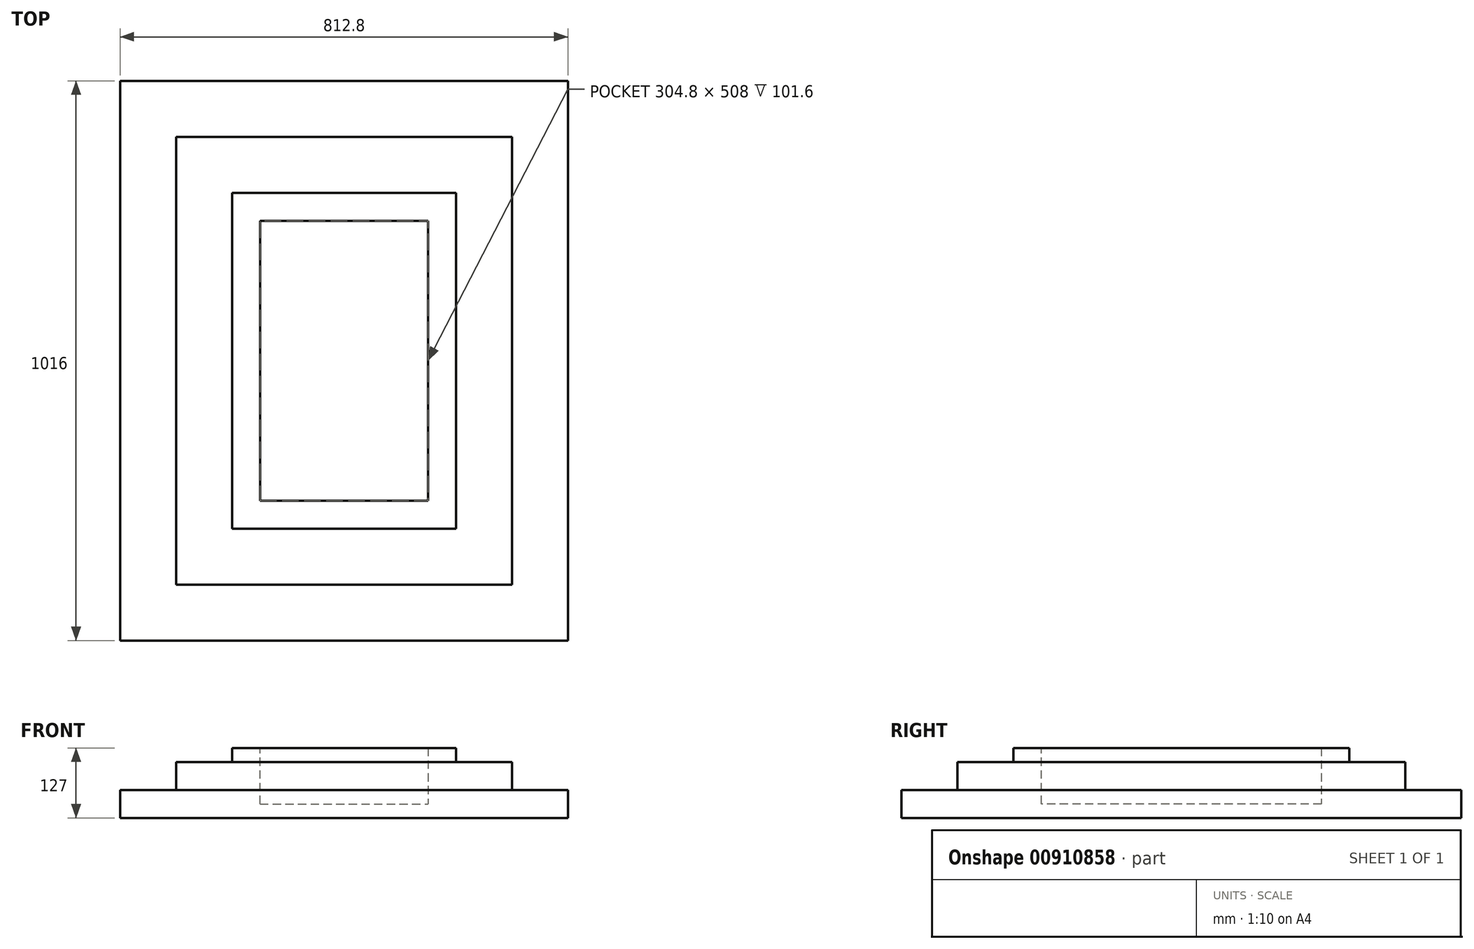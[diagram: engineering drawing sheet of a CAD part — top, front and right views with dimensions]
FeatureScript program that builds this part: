
annotation { "Feature Type Name" : "Feature", "Feature Type Description" : "" }
export const myFeature = defineFeature(function(context is Context, id is Id, definition is map)
    precondition{}
    {
        {
            var Q0;
            Q0=qCreatedBy(makeId("Front.planeOp"),FACE);
            var sketch = newSketch(context, id + "F0", { "sketchPlane" : qUnion([Q0])});
            skLineSegment(sketch, "E0.bottom", {"start": v(-203.2, -50.8) * mm, "end": v(203.2, -50.8) * mm});
            skLineSegment(sketch, "E0.top", {"start": v(-203.2, 50.8) * mm, "end": v(203.2, 50.8) * mm});
            skLineSegment(sketch, "E0.left", {"start": v(-203.2, -50.8) * mm, "end": v(-203.2, 50.8) * mm});
            skLineSegment(sketch, "E0.right", {"start": v(203.2, -50.8) * mm, "end": v(203.2, 50.8) * mm});
            skPoint(sketch, "E0.middle", {"position": v(0, 0) * mm});
            skSolve(sketch);
        }
        {
            var Q0;
            Q0 = qSketchRegion(id + "F0", true);
            extrude(context, id + "F1", {"entities" : qUnion([Q0]), "endBound" : BoundingType.SYMMETRIC, "depth" : 50.8 * mm, "offsetDistance" : 25.4 * mm});
        }
        {
            var Q0;
            Q0=makeQuery(id+"F1.opExtrude","CAP_FACE",FACE,{"disambiguationData":[OSD([sQuery(id+"F0.wireOp",EDGE,"E0.bottom"),sQuery(id+"F0.wireOp",EDGE,"E0.top"),sQuery(id+"F0.wireOp",EDGE,"E0.left"),sQuery(id+"F0.wireOp",EDGE,"E0.right")])],"isStart":true});
            var sketch = newSketch(context, id + "F2", { "sketchPlane" : qUnion([Q0])});
            skLineSegment(sketch, "E1.bottom", {"start": v(-203.2, 50.8) * mm, "end": v(-152.4, 50.8) * mm});
            skLineSegment(sketch, "E1.top", {"start": v(-203.2, -50.8) * mm, "end": v(-152.4, -50.8) * mm});
            skLineSegment(sketch, "E1.left", {"start": v(-203.2, 50.8) * mm, "end": v(-203.2, -50.8) * mm});
            skLineSegment(sketch, "E1.right", {"start": v(-152.4, 50.8) * mm, "end": v(-152.4, -50.8) * mm});
            skLineSegment(sketch, "E2.bottom", {"start": v(203.2, -50.8) * mm, "end": v(152.4, -50.8) * mm});
            skLineSegment(sketch, "E2.top", {"start": v(203.2, 50.8) * mm, "end": v(152.4, 50.8) * mm});
            skLineSegment(sketch, "E2.left", {"start": v(203.2, -50.8) * mm, "end": v(203.2, 50.8) * mm});
            skLineSegment(sketch, "E2.right", {"start": v(152.4, -50.8) * mm, "end": v(152.4, 50.8) * mm});
            skSolve(sketch);
        }
        {
            var Q0;
            Q0 = qSketchRegion(id + "F2", true);
            extrude(context, id + "F3", {"entities" : qUnion([Q0]), "operationType" : NewBodyOperationType.ADD, "depth" : 508 * mm, "offsetDistance" : 25.4 * mm});
        }
        {
            var Q0;
            Q0=makeQuery(id+"F3.opExtrude","CAP_FACE",FACE,{"disambiguationData":[OSD([sQuery(id+"F2.wireOp",EDGE,"E1.bottom"),sQuery(id+"F2.wireOp",EDGE,"E1.top"),sQuery(id+"F2.wireOp",EDGE,"E1.left"),sQuery(id+"F2.wireOp",EDGE,"E1.right")])],"isStart":false});
            var sketch = newSketch(context, id + "F4", { "sketchPlane" : qUnion([Q0])});
            skLineSegment(sketch, "E3.bottom", {"start": v(-203.2, 50.8) * mm, "end": v(203.2, 50.8) * mm});
            skLineSegment(sketch, "E3.top", {"start": v(-203.2, -50.8) * mm, "end": v(203.2, -50.8) * mm});
            skLineSegment(sketch, "E3.left", {"start": v(-203.2, 50.8) * mm, "end": v(-203.2, -50.8) * mm});
            skLineSegment(sketch, "E3.right", {"start": v(203.2, 50.8) * mm, "end": v(203.2, -50.8) * mm});
            skSolve(sketch);
        }
        {
            var Q0;
            Q0 = qSketchRegion(id + "F4", true);
            extrude(context, id + "F5", {"entities" : qUnion([Q0]), "operationType" : NewBodyOperationType.ADD, "depth" : 50.8 * mm, "offsetDistance" : 25.4 * mm});
        }
        {
            var Q0;
            Q0=makeQuery(id+"F5.boolean.opBoolean","MERGE",FACE,{"derivedFrom":[makeQuery(id+"F3.boolean.opBoolean","MERGE",FACE,{"derivedFrom":[makeQuery(id+"F1.opExtrude","SWEPT_FACE",FACE,{"disambiguationData":[OSD([sQuery(id+"F0.wireOp",EDGE,"E0.bottom")])]}),makeQuery(id+"F3.opExtrude","SWEPT_FACE",FACE,{"disambiguationData":[OSD([sQuery(id+"F2.wireOp",EDGE,"E1.top")])]}),makeQuery(id+"F3.opExtrude","SWEPT_FACE",FACE,{"disambiguationData":[OSD([sQuery(id+"F2.wireOp",EDGE,"E2.bottom")])]})]}),makeQuery(id+"F5.opExtrude","SWEPT_FACE",FACE,{"disambiguationData":[OSD([sQuery(id+"F4.wireOp",EDGE,"E3.top")])]})]});
            var sketch = newSketch(context, id + "F6", { "sketchPlane" : qUnion([Q0])});
            skLineSegment(sketch, "E4.bottom", {"start": v(-203.2, 25.4) * mm, "end": v(203.2, 25.4) * mm});
            skLineSegment(sketch, "E4.top", {"start": v(-203.2, -584.2) * mm, "end": v(203.2, -584.2) * mm});
            skLineSegment(sketch, "E4.left", {"start": v(-203.2, 25.4) * mm, "end": v(-203.2, -584.2) * mm});
            skLineSegment(sketch, "E4.right", {"start": v(203.2, 25.4) * mm, "end": v(203.2, -584.2) * mm});
            skSolve(sketch);
        }
        {
            var Q0;
            Q0 = qSketchRegion(id + "F6", true);
            extrude(context, id + "F7", {"entities" : qUnion([Q0]), "operationType" : NewBodyOperationType.ADD, "depth" : 25.4 * mm, "offsetDistance" : 25.4 * mm});
        }
        {
            var Q0;
            Q0=makeQuery(id+"F7.boolean.opBoolean","MERGE",FACE,{"derivedFrom":[makeQuery(id+"F1.opExtrude","CAP_FACE",FACE,{"disambiguationData":[OSD([sQuery(id+"F0.wireOp",EDGE,"E0.bottom"),sQuery(id+"F0.wireOp",EDGE,"E0.top"),sQuery(id+"F0.wireOp",EDGE,"E0.left"),sQuery(id+"F0.wireOp",EDGE,"E0.right")])],"isStart":false}),makeQuery(id+"F7.opExtrude","SWEPT_FACE",FACE,{"disambiguationData":[OSD([sQuery(id+"F6.wireOp",EDGE,"E4.bottom")])]})]});
            var sketch = newSketch(context, id + "F8", { "sketchPlane" : qUnion([Q0])});
            skLineSegment(sketch, "E5.bottom", {"start": v(-203.2, -76.2) * mm, "end": v(203.2, -76.2) * mm});
            skLineSegment(sketch, "E5.top", {"start": v(-203.2, -25.4) * mm, "end": v(203.2, -25.4) * mm});
            skLineSegment(sketch, "E5.left", {"start": v(-203.2, -76.2) * mm, "end": v(-203.2, -25.4) * mm});
            skLineSegment(sketch, "E5.right", {"start": v(203.2, -76.2) * mm, "end": v(203.2, -25.4) * mm});
            skLineSegment(sketch, "E6.top", {"start": v(-203.2, 25.4) * mm, "end": v(203.2, 25.4) * mm});
            skLineSegment(sketch, "E6.left", {"start": v(-203.2, -25.4) * mm, "end": v(-203.2, 25.4) * mm});
            skLineSegment(sketch, "E6.right", {"start": v(203.2, -25.4) * mm, "end": v(203.2, 25.4) * mm});
            skSolve(sketch);
        }
        {
            var Q0;
            Q0=makeQuery(id+"F8.imprint","IMPRINT",FACE,{"disambiguationData":[TD([[makeQuery(id+"F8.imprint","IMPRINT",EDGE,{"derivedFrom":sQuery(id+"F8.wireOp",EDGE,"E5.bottom")}),1.0]])]});
            extrude(context, id + "F9", {"entities" : qUnion([Q0]), "operationType" : NewBodyOperationType.ADD, "depth" : 203.2 * mm, "offsetDistance" : 25.4 * mm});
        }
        {
            var Q0;
            Q0=makeQuery(id+"F7.boolean.opBoolean","MERGE",FACE,{"derivedFrom":[makeQuery(id+"F1.opExtrude","CAP_FACE",FACE,{"disambiguationData":[OSD([sQuery(id+"F0.wireOp",EDGE,"E0.bottom"),sQuery(id+"F0.wireOp",EDGE,"E0.top"),sQuery(id+"F0.wireOp",EDGE,"E0.left"),sQuery(id+"F0.wireOp",EDGE,"E0.right")])],"isStart":false}),makeQuery(id+"F7.opExtrude","SWEPT_FACE",FACE,{"disambiguationData":[OSD([sQuery(id+"F6.wireOp",EDGE,"E4.bottom")])]})]});
            var sketch = newSketch(context, id + "F10", { "sketchPlane" : qUnion([Q0])});
            skLineSegment(sketch, "E7.bottom", {"start": v(-203.2, -25.4) * mm, "end": v(203.2, -25.4) * mm});
            skLineSegment(sketch, "E7.top", {"start": v(-203.2, 25.4) * mm, "end": v(203.2, 25.4) * mm});
            skLineSegment(sketch, "E7.left", {"start": v(-203.2, -25.4) * mm, "end": v(-203.2, 25.4) * mm});
            skLineSegment(sketch, "E7.right", {"start": v(203.2, -25.4) * mm, "end": v(203.2, 25.4) * mm});
            skSolve(sketch);
        }
        {
            var Q0;
            Q0 = qSketchRegion(id + "F10", true);
            extrude(context, id + "F11", {"entities" : qUnion([Q0]), "operationType" : NewBodyOperationType.ADD, "depth" : 101.6 * mm, "offsetDistance" : 25.4 * mm});
        }
        {
            var Q0;
            Q0=makeQuery(id+"F7.boolean.opBoolean","MERGE",FACE,{"derivedFrom":[makeQuery(id+"F5.opExtrude","CAP_FACE",FACE,{"disambiguationData":[OSD([sQuery(id+"F4.wireOp",EDGE,"E3.bottom"),sQuery(id+"F4.wireOp",EDGE,"E3.top"),sQuery(id+"F4.wireOp",EDGE,"E3.left"),sQuery(id+"F4.wireOp",EDGE,"E3.right")])],"isStart":false}),makeQuery(id+"F7.opExtrude","SWEPT_FACE",FACE,{"disambiguationData":[OSD([sQuery(id+"F6.wireOp",EDGE,"E4.top")])]})]});
            var sketch = newSketch(context, id + "F12", { "sketchPlane" : qUnion([Q0])});
            skLineSegment(sketch, "E8.bottom", {"start": v(-203.2, -76.2) * mm, "end": v(203.2, -76.2) * mm});
            skLineSegment(sketch, "E8.top", {"start": v(-203.2, -25.4) * mm, "end": v(203.2, -25.4) * mm});
            skLineSegment(sketch, "E8.left", {"start": v(-203.2, -76.2) * mm, "end": v(-203.2, -25.4) * mm});
            skLineSegment(sketch, "E8.right", {"start": v(203.2, -76.2) * mm, "end": v(203.2, -25.4) * mm});
            skSolve(sketch);
        }
        {
            var Q0;
            Q0=makeQuery(id+"F12.imprint","IMPRINT",FACE,{"disambiguationData":[TD([[makeQuery(id+"F12.imprint","IMPRINT",EDGE,{"derivedFrom":sQuery(id+"F12.wireOp",EDGE,"E8.bottom")}),1.0]])]});
            extrude(context, id + "F13", {"entities" : qUnion([Q0]), "operationType" : NewBodyOperationType.ADD, "depth" : 203.2 * mm, "offsetDistance" : 25.4 * mm});
        }
        {
            var Q0;
            Q0=makeQuery(id+"F7.boolean.opBoolean","MERGE",FACE,{"derivedFrom":[makeQuery(id+"F5.opExtrude","CAP_FACE",FACE,{"disambiguationData":[OSD([sQuery(id+"F4.wireOp",EDGE,"E3.bottom"),sQuery(id+"F4.wireOp",EDGE,"E3.top"),sQuery(id+"F4.wireOp",EDGE,"E3.left"),sQuery(id+"F4.wireOp",EDGE,"E3.right")])],"isStart":false}),makeQuery(id+"F7.opExtrude","SWEPT_FACE",FACE,{"disambiguationData":[OSD([sQuery(id+"F6.wireOp",EDGE,"E4.top")])]})]});
            var sketch = newSketch(context, id + "F14", { "sketchPlane" : qUnion([Q0])});
            skLineSegment(sketch, "E9.bottom", {"start": v(-203.2, -25.4) * mm, "end": v(203.2, -25.4) * mm});
            skLineSegment(sketch, "E9.top", {"start": v(-203.2, 25.4) * mm, "end": v(203.2, 25.4) * mm});
            skLineSegment(sketch, "E9.left", {"start": v(-203.2, -25.4) * mm, "end": v(-203.2, 25.4) * mm});
            skLineSegment(sketch, "E9.right", {"start": v(203.2, -25.4) * mm, "end": v(203.2, 25.4) * mm});
            skSolve(sketch);
        }
        {
            var Q0;
            Q0 = qSketchRegion(id + "F14", true);
            extrude(context, id + "F15", {"entities" : qUnion([Q0]), "operationType" : NewBodyOperationType.ADD, "depth" : 101.6 * mm, "offsetDistance" : 25.4 * mm});
        }
        {
            var Q0;
            Q0=makeQuery(id+"F15.boolean.opBoolean","MERGE",FACE,{"derivedFrom":[makeQuery(id+"F13.boolean.opBoolean","MERGE",FACE,{"derivedFrom":[makeQuery(id+"F11.boolean.opBoolean","MERGE",FACE,{"derivedFrom":[makeQuery(id+"F9.boolean.opBoolean","MERGE",FACE,{"derivedFrom":[makeQuery(id+"F7.boolean.opBoolean","MERGE",FACE,{"derivedFrom":[makeQuery(id+"F5.boolean.opBoolean","MERGE",FACE,{"derivedFrom":[makeQuery(id+"F3.boolean.opBoolean","MERGE",FACE,{"derivedFrom":[makeQuery(id+"F1.opExtrude","SWEPT_FACE",FACE,{"disambiguationData":[OSD([sQuery(id+"F0.wireOp",EDGE,"E0.right")])]}),makeQuery(id+"F3.opExtrude","SWEPT_FACE",FACE,{"disambiguationData":[OSD([sQuery(id+"F2.wireOp",EDGE,"E1.left")])]})]}),makeQuery(id+"F5.opExtrude","SWEPT_FACE",FACE,{"disambiguationData":[OSD([sQuery(id+"F4.wireOp",EDGE,"E3.left")])]})]}),makeQuery(id+"F7.opExtrude","SWEPT_FACE",FACE,{"disambiguationData":[OSD([sQuery(id+"F6.wireOp",EDGE,"E4.right")])]})]}),makeQuery(id+"F9.opExtrude","SWEPT_FACE",FACE,{"disambiguationData":[OSD([sQuery(id+"F8.wireOp",EDGE,"E5.right")])]})]}),makeQuery(id+"F11.opExtrude","SWEPT_FACE",FACE,{"disambiguationData":[OSD([sQuery(id+"F10.wireOp",EDGE,"E7.right")])]})]}),makeQuery(id+"F13.opExtrude","SWEPT_FACE",FACE,{"disambiguationData":[OSD([sQuery(id+"F12.wireOp",EDGE,"E8.left")])]})]}),makeQuery(id+"F15.opExtrude","SWEPT_FACE",FACE,{"disambiguationData":[OSD([sQuery(id+"F14.wireOp",EDGE,"E9.left")])]})]});
            var sketch = newSketch(context, id + "F16", { "sketchPlane" : qUnion([Q0])});
            skLineSegment(sketch, "E10.bottom", {"start": v(-228.6, -25.4) * mm, "end": v(787.4, -25.4) * mm});
            skLineSegment(sketch, "E10.top", {"start": v(-228.6, -76.2) * mm, "end": v(787.4, -76.2) * mm});
            skLineSegment(sketch, "E10.left", {"start": v(-228.6, -25.4) * mm, "end": v(-228.6, -76.2) * mm});
            skLineSegment(sketch, "E10.right", {"start": v(787.4, -25.4) * mm, "end": v(787.4, -76.2) * mm});
            skSolve(sketch);
        }
        {
            var Q0;
            Q0=makeQuery(id+"F16.imprint","IMPRINT",FACE,{"disambiguationData":[TD([[makeQuery(id+"F16.imprint","IMPRINT",EDGE,{"derivedFrom":sQuery(id+"F16.wireOp",EDGE,"E10.top")}),1.0]])]});
            extrude(context, id + "F17", {"entities" : qUnion([Q0]), "operationType" : NewBodyOperationType.ADD, "depth" : 203.2 * mm, "offsetDistance" : 25.4 * mm});
        }
        {
            var Q0;
            Q0=makeQuery(id+"F15.boolean.opBoolean","MERGE",FACE,{"derivedFrom":[makeQuery(id+"F13.boolean.opBoolean","MERGE",FACE,{"derivedFrom":[makeQuery(id+"F11.boolean.opBoolean","MERGE",FACE,{"derivedFrom":[makeQuery(id+"F9.boolean.opBoolean","MERGE",FACE,{"derivedFrom":[makeQuery(id+"F7.boolean.opBoolean","MERGE",FACE,{"derivedFrom":[makeQuery(id+"F5.boolean.opBoolean","MERGE",FACE,{"derivedFrom":[makeQuery(id+"F3.boolean.opBoolean","MERGE",FACE,{"derivedFrom":[makeQuery(id+"F1.opExtrude","SWEPT_FACE",FACE,{"disambiguationData":[OSD([sQuery(id+"F0.wireOp",EDGE,"E0.right")])]}),makeQuery(id+"F3.opExtrude","SWEPT_FACE",FACE,{"disambiguationData":[OSD([sQuery(id+"F2.wireOp",EDGE,"E1.left")])]})]}),makeQuery(id+"F5.opExtrude","SWEPT_FACE",FACE,{"disambiguationData":[OSD([sQuery(id+"F4.wireOp",EDGE,"E3.left")])]})]}),makeQuery(id+"F7.opExtrude","SWEPT_FACE",FACE,{"disambiguationData":[OSD([sQuery(id+"F6.wireOp",EDGE,"E4.right")])]})]}),makeQuery(id+"F9.opExtrude","SWEPT_FACE",FACE,{"disambiguationData":[OSD([sQuery(id+"F8.wireOp",EDGE,"E5.right")])]})]}),makeQuery(id+"F11.opExtrude","SWEPT_FACE",FACE,{"disambiguationData":[OSD([sQuery(id+"F10.wireOp",EDGE,"E7.right")])]})]}),makeQuery(id+"F13.opExtrude","SWEPT_FACE",FACE,{"disambiguationData":[OSD([sQuery(id+"F12.wireOp",EDGE,"E8.left")])]})]}),makeQuery(id+"F15.opExtrude","SWEPT_FACE",FACE,{"disambiguationData":[OSD([sQuery(id+"F14.wireOp",EDGE,"E9.left")])]})]});
            var sketch = newSketch(context, id + "F18", { "sketchPlane" : qUnion([Q0])});
            skLineSegment(sketch, "E11.bottom", {"start": v(-127, 25.4) * mm, "end": v(685.8, 25.4) * mm});
            skLineSegment(sketch, "E11.top", {"start": v(-127, -25.4) * mm, "end": v(685.8, -25.4) * mm});
            skLineSegment(sketch, "E11.left", {"start": v(-127, 25.4) * mm, "end": v(-127, -25.4) * mm});
            skLineSegment(sketch, "E11.right", {"start": v(685.8, 25.4) * mm, "end": v(685.8, -25.4) * mm});
            skSolve(sketch);
        }
        {
            var Q0;
            Q0 = qSketchRegion(id + "F18", true);
            extrude(context, id + "F19", {"entities" : qUnion([Q0]), "operationType" : NewBodyOperationType.ADD, "depth" : 101.6 * mm, "offsetDistance" : 25.4 * mm});
        }
        {
            var Q0;
            Q0=makeQuery(id+"F15.boolean.opBoolean","MERGE",FACE,{"derivedFrom":[makeQuery(id+"F13.boolean.opBoolean","MERGE",FACE,{"derivedFrom":[makeQuery(id+"F11.boolean.opBoolean","MERGE",FACE,{"derivedFrom":[makeQuery(id+"F9.boolean.opBoolean","MERGE",FACE,{"derivedFrom":[makeQuery(id+"F7.boolean.opBoolean","MERGE",FACE,{"derivedFrom":[makeQuery(id+"F5.boolean.opBoolean","MERGE",FACE,{"derivedFrom":[makeQuery(id+"F3.boolean.opBoolean","MERGE",FACE,{"derivedFrom":[makeQuery(id+"F1.opExtrude","SWEPT_FACE",FACE,{"disambiguationData":[OSD([sQuery(id+"F0.wireOp",EDGE,"E0.left")])]}),makeQuery(id+"F3.opExtrude","SWEPT_FACE",FACE,{"disambiguationData":[OSD([sQuery(id+"F2.wireOp",EDGE,"E2.left")])]})]}),makeQuery(id+"F5.opExtrude","SWEPT_FACE",FACE,{"disambiguationData":[OSD([sQuery(id+"F4.wireOp",EDGE,"E3.right")])]})]}),makeQuery(id+"F7.opExtrude","SWEPT_FACE",FACE,{"disambiguationData":[OSD([sQuery(id+"F6.wireOp",EDGE,"E4.left")])]})]}),makeQuery(id+"F9.opExtrude","SWEPT_FACE",FACE,{"disambiguationData":[OSD([sQuery(id+"F8.wireOp",EDGE,"E5.left")])]})]}),makeQuery(id+"F11.opExtrude","SWEPT_FACE",FACE,{"disambiguationData":[OSD([sQuery(id+"F10.wireOp",EDGE,"E7.left")])]})]}),makeQuery(id+"F13.opExtrude","SWEPT_FACE",FACE,{"disambiguationData":[OSD([sQuery(id+"F12.wireOp",EDGE,"E8.right")])]})]}),makeQuery(id+"F15.opExtrude","SWEPT_FACE",FACE,{"disambiguationData":[OSD([sQuery(id+"F14.wireOp",EDGE,"E9.right")])]})]});
            var sketch = newSketch(context, id + "F20", { "sketchPlane" : qUnion([Q0])});
            skLineSegment(sketch, "E12.bottom", {"start": v(-787.4, -25.4) * mm, "end": v(228.6, -25.4) * mm});
            skLineSegment(sketch, "E12.top", {"start": v(-787.4, -76.2) * mm, "end": v(228.6, -76.2) * mm});
            skLineSegment(sketch, "E12.left", {"start": v(-787.4, -25.4) * mm, "end": v(-787.4, -76.2) * mm});
            skLineSegment(sketch, "E12.right", {"start": v(228.6, -25.4) * mm, "end": v(228.6, -76.2) * mm});
            skSolve(sketch);
        }
        {
            var Q0;
            Q0 = qSketchRegion(id + "F20", true);
            extrude(context, id + "F21", {"entities" : qUnion([Q0]), "operationType" : NewBodyOperationType.ADD, "depth" : 203.2 * mm, "offsetDistance" : 25.4 * mm});
        }
        {
            var Q0;
            Q0=makeQuery(id+"F15.boolean.opBoolean","MERGE",FACE,{"derivedFrom":[makeQuery(id+"F13.boolean.opBoolean","MERGE",FACE,{"derivedFrom":[makeQuery(id+"F11.boolean.opBoolean","MERGE",FACE,{"derivedFrom":[makeQuery(id+"F9.boolean.opBoolean","MERGE",FACE,{"derivedFrom":[makeQuery(id+"F7.boolean.opBoolean","MERGE",FACE,{"derivedFrom":[makeQuery(id+"F5.boolean.opBoolean","MERGE",FACE,{"derivedFrom":[makeQuery(id+"F3.boolean.opBoolean","MERGE",FACE,{"derivedFrom":[makeQuery(id+"F1.opExtrude","SWEPT_FACE",FACE,{"disambiguationData":[OSD([sQuery(id+"F0.wireOp",EDGE,"E0.left")])]}),makeQuery(id+"F3.opExtrude","SWEPT_FACE",FACE,{"disambiguationData":[OSD([sQuery(id+"F2.wireOp",EDGE,"E2.left")])]})]}),makeQuery(id+"F5.opExtrude","SWEPT_FACE",FACE,{"disambiguationData":[OSD([sQuery(id+"F4.wireOp",EDGE,"E3.right")])]})]}),makeQuery(id+"F7.opExtrude","SWEPT_FACE",FACE,{"disambiguationData":[OSD([sQuery(id+"F6.wireOp",EDGE,"E4.left")])]})]}),makeQuery(id+"F9.opExtrude","SWEPT_FACE",FACE,{"disambiguationData":[OSD([sQuery(id+"F8.wireOp",EDGE,"E5.left")])]})]}),makeQuery(id+"F11.opExtrude","SWEPT_FACE",FACE,{"disambiguationData":[OSD([sQuery(id+"F10.wireOp",EDGE,"E7.left")])]})]}),makeQuery(id+"F13.opExtrude","SWEPT_FACE",FACE,{"disambiguationData":[OSD([sQuery(id+"F12.wireOp",EDGE,"E8.right")])]})]}),makeQuery(id+"F15.opExtrude","SWEPT_FACE",FACE,{"disambiguationData":[OSD([sQuery(id+"F14.wireOp",EDGE,"E9.right")])]})]});
            var sketch = newSketch(context, id + "F22", { "sketchPlane" : qUnion([Q0])});
            skLineSegment(sketch, "E13.bottom", {"start": v(-685.8, 25.4) * mm, "end": v(127, 25.4) * mm});
            skLineSegment(sketch, "E13.top", {"start": v(-685.8, -25.4) * mm, "end": v(127, -25.4) * mm});
            skLineSegment(sketch, "E13.left", {"start": v(-685.8, 25.4) * mm, "end": v(-685.8, -25.4) * mm});
            skLineSegment(sketch, "E13.right", {"start": v(127, 25.4) * mm, "end": v(127, -25.4) * mm});
            skSolve(sketch);
        }
        {
            var Q0;
            Q0 = qSketchRegion(id + "F22", true);
            extrude(context, id + "F23", {"entities" : qUnion([Q0]), "operationType" : NewBodyOperationType.ADD, "depth" : 101.6 * mm, "offsetDistance" : 25.4 * mm});
        }
    });
